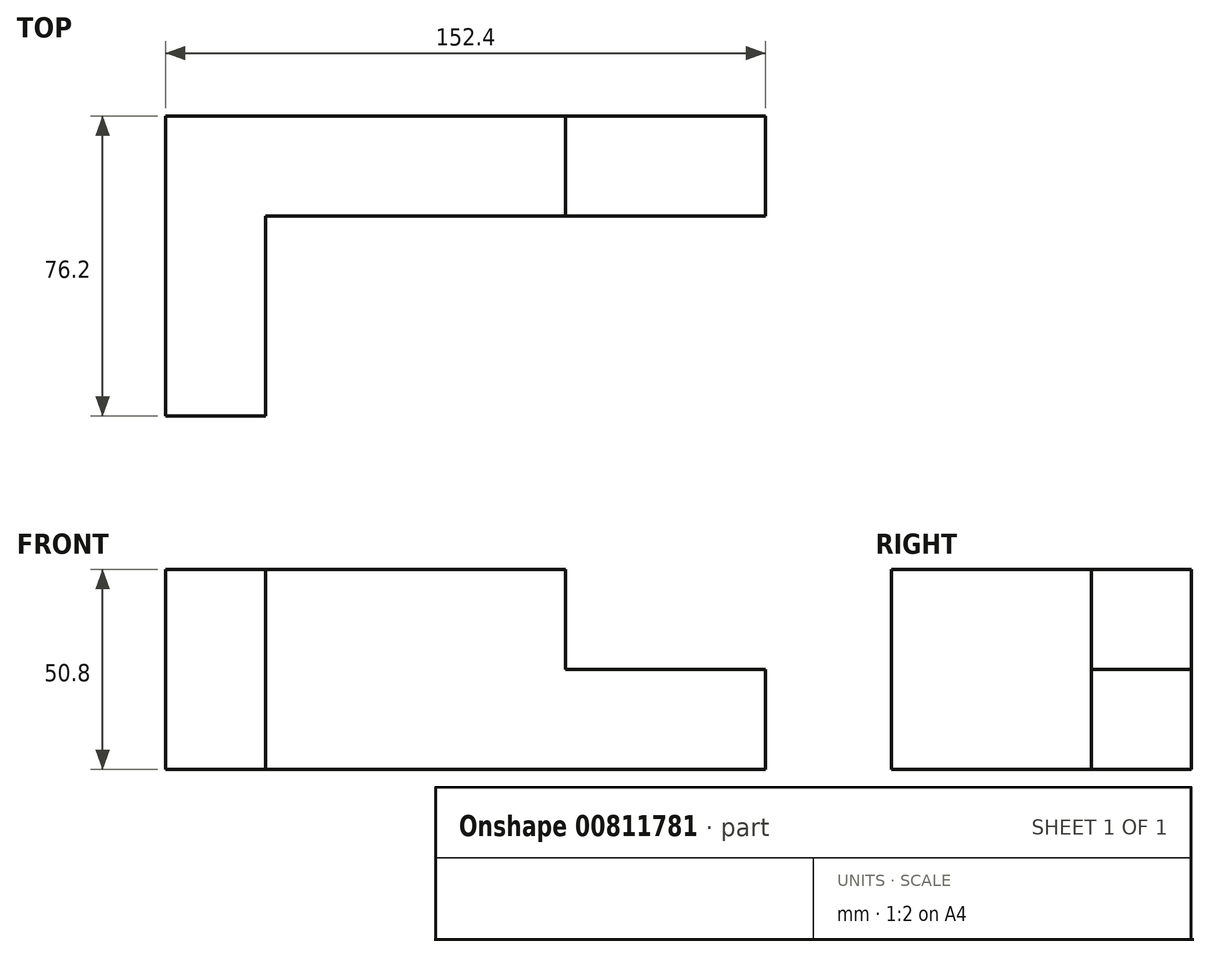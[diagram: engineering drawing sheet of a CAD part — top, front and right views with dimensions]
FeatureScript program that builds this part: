
annotation { "Feature Type Name" : "Feature", "Feature Type Description" : "" }
export const myFeature = defineFeature(function(context is Context, id is Id, definition is map)
    precondition{}
    {
        {
            var Q0;
            Q0=qCreatedBy(makeId("Front.planeOp"),FACE);
            var sketch = newSketch(context, id + "F0", { "sketchPlane" : qUnion([Q0])});
            skLineSegment(sketch, "E0", {"start": v(0, 0) * mm, "end": v(152.4, 0) * mm});
            skLineSegment(sketch, "E1", {"start": v(152.4, 0) * mm, "end": v(152.4, 50.8) * mm});
            skLineSegment(sketch, "E2", {"start": v(152.4, 50.8) * mm, "end": v(0, 50.8) * mm});
            skLineSegment(sketch, "E3", {"start": v(0, 50.8) * mm, "end": v(0, 0) * mm});
            skSolve(sketch);
        }
        {
            var Q0;
            Q0=makeQuery(id+"F0.imprint","IMPRINT",FACE,{"disambiguationData":[TD([[makeQuery(id+"F0.imprint","IMPRINT",EDGE,{"derivedFrom":sQuery(id+"F0.wireOp",EDGE,"E0")}),1.0]])]});
            extrude(context, id + "F1", {"entities" : qUnion([Q0]), "depth" : 76.2 * mm, "offsetDistance" : 25.4 * mm});
        }
        {
            var Q0;
            Q0=makeQuery(id+"F1.opExtrude","CAP_FACE",FACE,{"disambiguationData":[OSD([sQuery(id+"F0.wireOp",EDGE,"E0"),sQuery(id+"F0.wireOp",EDGE,"E1"),sQuery(id+"F0.wireOp",EDGE,"E2"),sQuery(id+"F0.wireOp",EDGE,"E3")])],"isStart":false});
            var sketch = newSketch(context, id + "F2", { "sketchPlane" : qUnion([Q0])});
            skLineSegment(sketch, "E4", {"start": v(152.4, 0) * mm, "end": v(25.4, 0) * mm});
            skSolve(sketch);
        }
        {
            var Q0;
            {var subQ2=sQuery(id+"F2.wireOp",EDGE,"E4");Q0=makeQuery(id+"F2.imprint","IMPRINT",FACE,{"disambiguationData":[TD([[makeQuery(id+"F2.imprint","IMPRINT",EDGE,{"derivedFrom":subQ2}),1.0]])]});}
            var sketch = newSketch(context, id + "F3", { "sketchPlane" : qUnion([Q0])});
            skLineSegment(sketch, "E5", {"start": v(152.45, 0) * mm, "end": v(25.45, 0) * mm});
            skLineSegment(sketch, "E6", {"start": v(25.45, 0) * mm, "end": v(25.45, 50.86) * mm});
            skLineSegment(sketch, "E7.bottom", {"start": v(25.45, 50.86) * mm, "end": v(152.45, 50.86) * mm});
            skLineSegment(sketch, "E7.top", {"start": v(25.45, 0) * mm, "end": v(152.45, 0) * mm});
            skLineSegment(sketch, "E7.left", {"start": v(25.45, 50.86) * mm, "end": v(25.45, 0) * mm});
            skLineSegment(sketch, "E7.right", {"start": v(152.45, 50.86) * mm, "end": v(152.45, 0) * mm});
            skSolve(sketch);
        }
        {
            var Q0;
            Q0 = qSketchRegion(id + "F3", true);
            var Q1;
            {var subQ1=makeQuery(id+"F2.imprint","IMPRINT",EDGE,{"derivedFrom":makeQuery(id+"F1.opExtrude","CAP_EDGE",EDGE,{"disambiguationData":[OSD([sQuery(id+"F0.wireOp",EDGE,"E1")])],"isStart":false})});Q1=makeQuery(id+"F3.imprint","IMPRINT",FACE,{"disambiguationData":[TD([[makeQuery(id+"F3.imprint","IMPRINT",EDGE,{"derivedFrom":subQ1}),1.0]])]});}
            extrude(context, id + "F4", {"entities" : qUnion([Q0, Q1]), "operationType" : NewBodyOperationType.REMOVE, "oppositeDirection" : true, "depth" : 50.8 * mm, "offsetDistance" : 25.4 * mm});
        }
        {
            var Q0;
            Q0=makeQuery(id+"F4.boolean.opBoolean","COPY",FACE,{"derivedFrom":makeQuery(id+"F4.opExtrude","CAP_FACE",FACE,{"disambiguationData":[OSD([sQuery(id+"F3.wireOp",EDGE,"E7.bottom"),sQuery(id+"F3.wireOp",EDGE,"E7.top"),sQuery(id+"F3.wireOp",EDGE,"E7.left"),sQuery(id+"F3.wireOp",EDGE,"E7.right")])],"isStart":false})});
            var sketch = newSketch(context, id + "F5", { "sketchPlane" : qUnion([Q0])});
            skLineSegment(sketch, "E8", {"start": v(152.4, 50.8) * mm, "end": v(101.6, 50.8) * mm});
            skLineSegment(sketch, "E9", {"start": v(101.6, 50.8) * mm, "end": v(101.6, 25.4) * mm});
            skLineSegment(sketch, "E10", {"start": v(101.6, 25.4) * mm, "end": v(152.4, 25.4) * mm});
            skSolve(sketch);
        }
        {
            var Q0;
            Q0 = qSketchRegion(id + "F5", true);
            var Q1;
            {var subQ0=sQuery(id+"F5.wireOp",EDGE,"E8");Q1=makeQuery(id+"F5.imprint","IMPRINT",FACE,{"disambiguationData":[TD([[makeQuery(id+"F5.imprint","IMPRINT",EDGE,{"derivedFrom":subQ0}),1.0]])]});}
            extrude(context, id + "F6", {"entities" : qUnion([Q0, Q1]), "operationType" : NewBodyOperationType.REMOVE, "oppositeDirection" : true, "depth" : 25.4 * mm, "offsetDistance" : 25.4 * mm});
        }
    });
